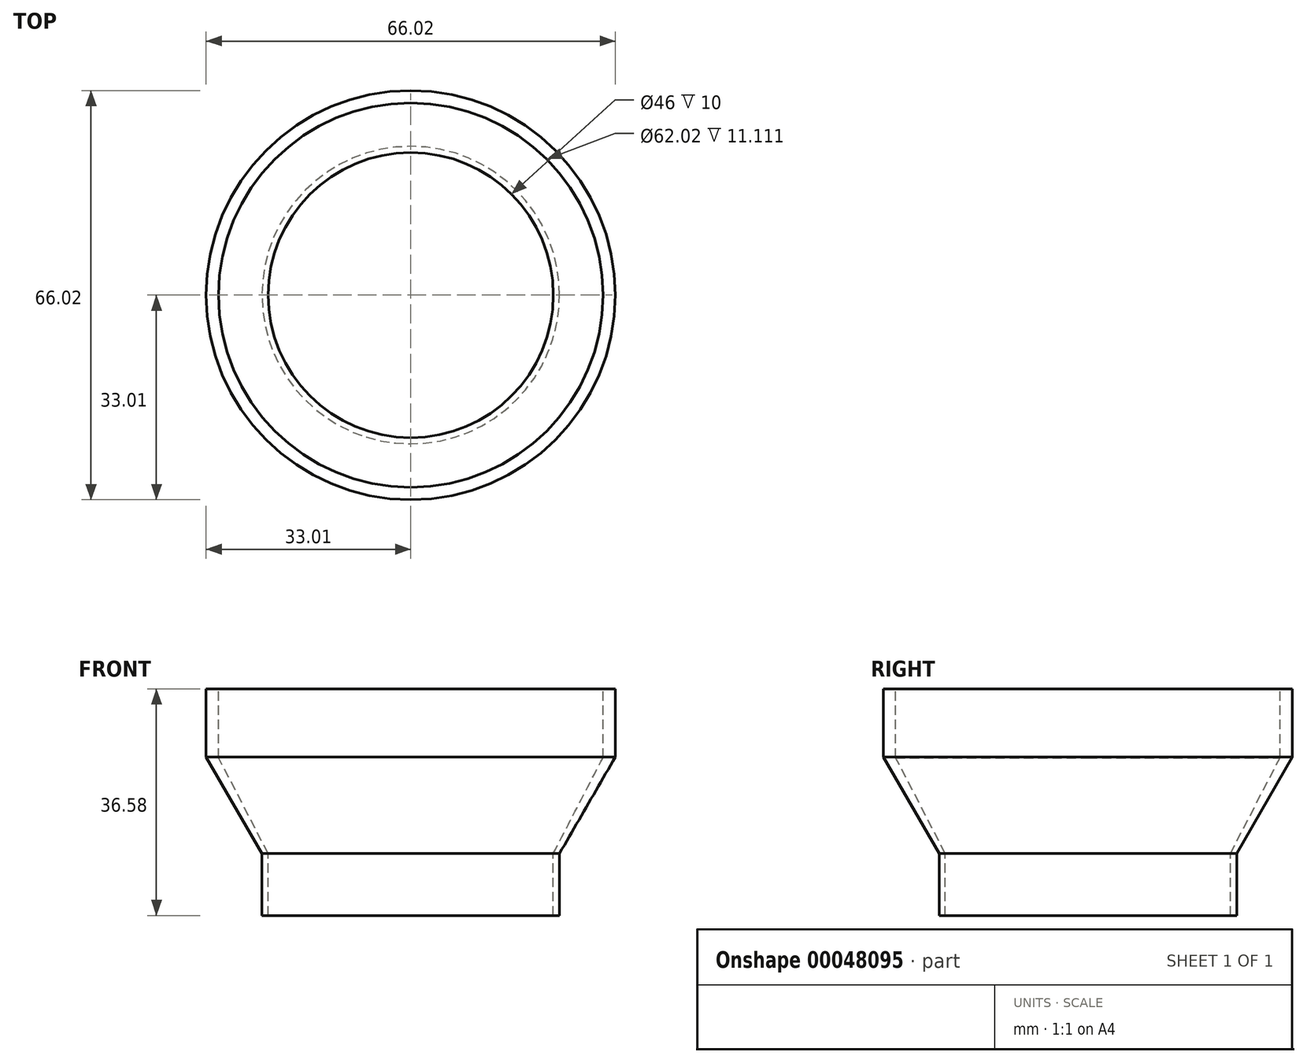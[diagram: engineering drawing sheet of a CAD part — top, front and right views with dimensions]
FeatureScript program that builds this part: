
annotation { "Feature Type Name" : "Feature", "Feature Type Description" : "" }
export const myFeature = defineFeature(function(context is Context, id is Id, definition is map)
    precondition{}
    {
        {
            var Q0;
            Q0=qCreatedBy(makeId("Top.planeOp"),FACE);
            var sketch = newSketch(context, id + "F0", { "sketchPlane" : qUnion([Q0])});
            skCircle(sketch, "E0", {"center": v(0, 0) * mm, "radius": 24 * mm});
            skSolve(sketch);
        }
        {
            var Q0;
            Q0=makeQuery(id+"F0.imprint","IMPRINT",FACE,{"disambiguationData":[TD([[makeQuery(id+"F0.imprint","IMPRINT",EDGE,{"derivedFrom":sQuery(id+"F0.wireOp",EDGE,"E0")}),1.0]])]});
            extrude(context, id + "F1", {"entities" : qUnion([Q0]), "depth" : 10 * mm});
        }
        {
            var Q0;
            Q0=makeQuery(id+"F1.opExtrude","CAP_FACE",FACE,{"disambiguationData":[OSD([sQuery(id+"F0.wireOp",EDGE,"E0")])],"isStart":false});
            var sketch = newSketch(context, id + "F2", { "sketchPlane" : qUnion([Q0])});
            skCircle(sketch, "E1", {"center": v(0, 0) * mm, "radius": 23 * mm});
            skSolve(sketch);
        }
        {
            var Q0;
            Q0=qSketchRegion(id+"F2",true);
            extrude(context, id + "F3", {"entities" : qUnion([Q0]), "operationType" : NewBodyOperationType.REMOVE, "endBound" : BoundingType.THROUGH_ALL, "oppositeDirection" : true, "depth" : 25 * mm});
        }
        {
            var Q0;
            Q0=qCreatedBy(makeId("Front.planeOp"),FACE);
            var sketch = newSketch(context, id + "F4", { "sketchPlane" : qUnion([Q0])});
            skLineSegment(sketch, "E2", {"start": v(-31.01, 25.47) * mm, "end": v(-31.01, 36.58) * mm});
            skLineSegment(sketch, "E3", {"start": v(-31.01, 36.58) * mm, "end": v(-33.01, 36.58) * mm});
            skLineSegment(sketch, "E4", {"start": v(-33.01, 36.58) * mm, "end": v(-33.01, 25.58) * mm});
            skLineSegment(sketch, "E5", {"start": v(-33.01, 25.58) * mm, "end": v(-24, 10) * mm});
            skLineSegment(sketch, "E6", {"start": v(-24, 10) * mm, "end": v(-23, 10) * mm});
            skLineSegment(sketch, "E7", {"start": v(-23, 10) * mm, "end": v(-31.01, 25.47) * mm});
            skLineSegment(sketch, "E8.0", {"start": v(-24, 10) * mm, "end": v(24, 10) * mm});
            skSolve(sketch);
        }
        {
            var Q0;
            Q0=qSketchRegion(id+"F4",true);
            var Q1;
            Q1=makeQuery(id+"F3.boolean.opBoolean","COPY",FACE,{"derivedFrom":makeQuery(id+"F3.opExtrude","SWEPT_FACE",FACE,{"disambiguationData":[OSD([sQuery(id+"F2.wireOp",EDGE,"E1")])]})});
            revolve(context, id + "F5", {"operationType" : NewBodyOperationType.ADD, "entities" : qUnion([Q0]), "axis" : qUnion([Q1]), "revolveType" : RevolveType.FULL});
        }
    });
